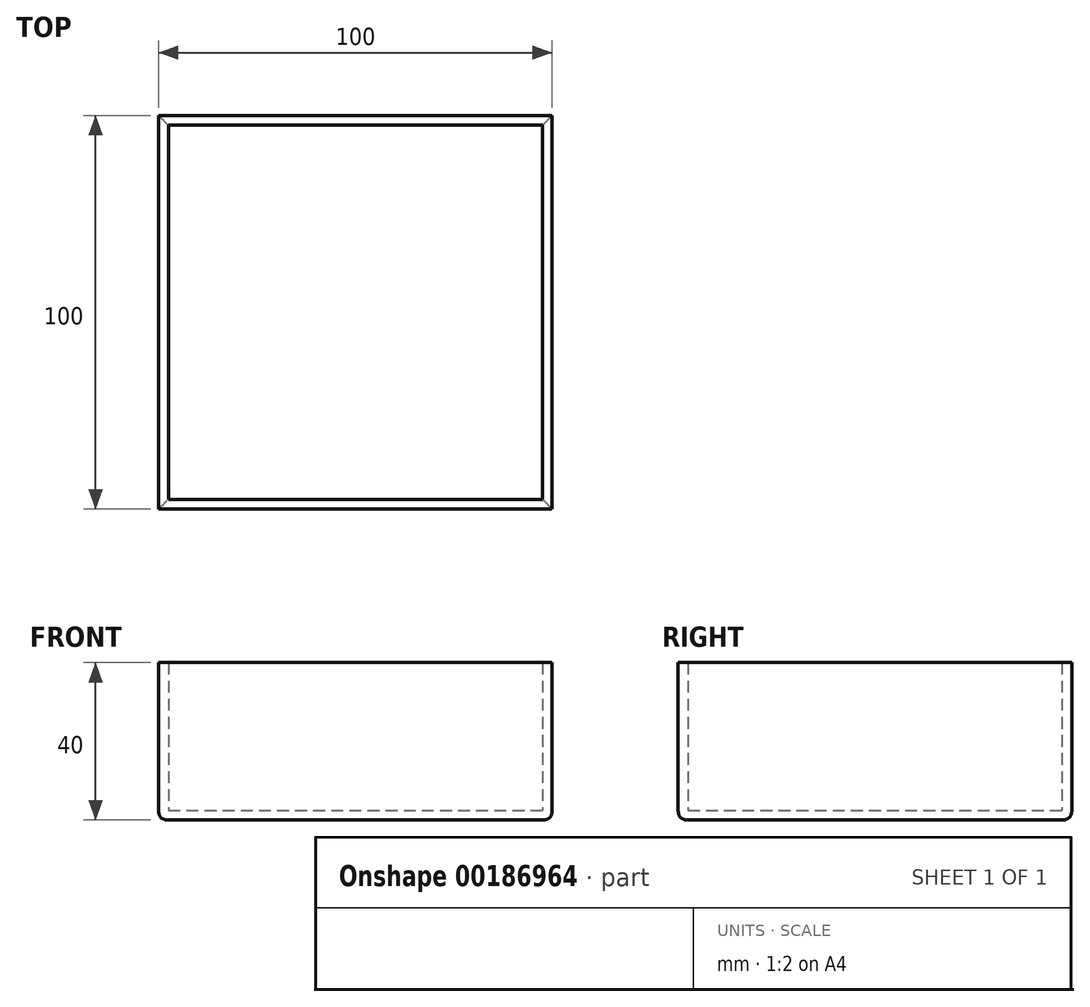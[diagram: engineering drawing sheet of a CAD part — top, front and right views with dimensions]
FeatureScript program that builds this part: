
annotation { "Feature Type Name" : "Feature", "Feature Type Description" : "" }
export const myFeature = defineFeature(function(context is Context, id is Id, definition is map)
    precondition{}
    {
        {
            var Q0;
            Q0=qCreatedBy(makeId("Top.planeOp"),FACE);
            var sketch = newSketch(context, id + "F0", { "sketchPlane" : qUnion([Q0])});
            skLineSegment(sketch, "E0.bottom", {"start": v(50, -50) * mm, "end": v(-50, -50) * mm});
            skLineSegment(sketch, "E0.top", {"start": v(50, 50) * mm, "end": v(-50, 50) * mm});
            skLineSegment(sketch, "E0.left", {"start": v(50, -50) * mm, "end": v(50, 50) * mm});
            skLineSegment(sketch, "E0.right", {"start": v(-50, -50) * mm, "end": v(-50, 50) * mm});
            skPoint(sketch, "E0.middle", {"position": v(0, 0) * mm});
            skSolve(sketch);
        }
        {
            var Q0;
            Q0 = qSketchRegion(id + "F0", true);
            extrude(context, id + "F1", {"entities" : qUnion([Q0]), "depth" : 40 * mm});
        }
        {
            var Q0;
            Q0=makeQuery(id+"F1.opExtrude","CAP_FACE",FACE,{"disambiguationData":[OSD([sQuery(id+"F0.wireOp",EDGE,"E0.bottom"),sQuery(id+"F0.wireOp",EDGE,"E0.top"),sQuery(id+"F0.wireOp",EDGE,"E0.left"),sQuery(id+"F0.wireOp",EDGE,"E0.right")])],"isStart":true});
            fillet(context, id + "F2", {"entities" : qUnion([Q0]), "radius" : 2.5 * mm, "tangentPropagation" : true, "rho" : 0.5, "crossSection" : FilletCrossSection.CONIC, "allowEdgeOverflow" : false});
        }
        {
            var Q0;
            Q0=makeQuery(id+"F1.opExtrude","CAP_FACE",FACE,{"disambiguationData":[OSD([sQuery(id+"F0.wireOp",EDGE,"E0.bottom"),sQuery(id+"F0.wireOp",EDGE,"E0.top"),sQuery(id+"F0.wireOp",EDGE,"E0.left"),sQuery(id+"F0.wireOp",EDGE,"E0.right")])],"isStart":false});
            shell(context, id + "F3", {"entities" : qUnion([Q0]), "thickness" : 2.5 * mm});
        }
    });
